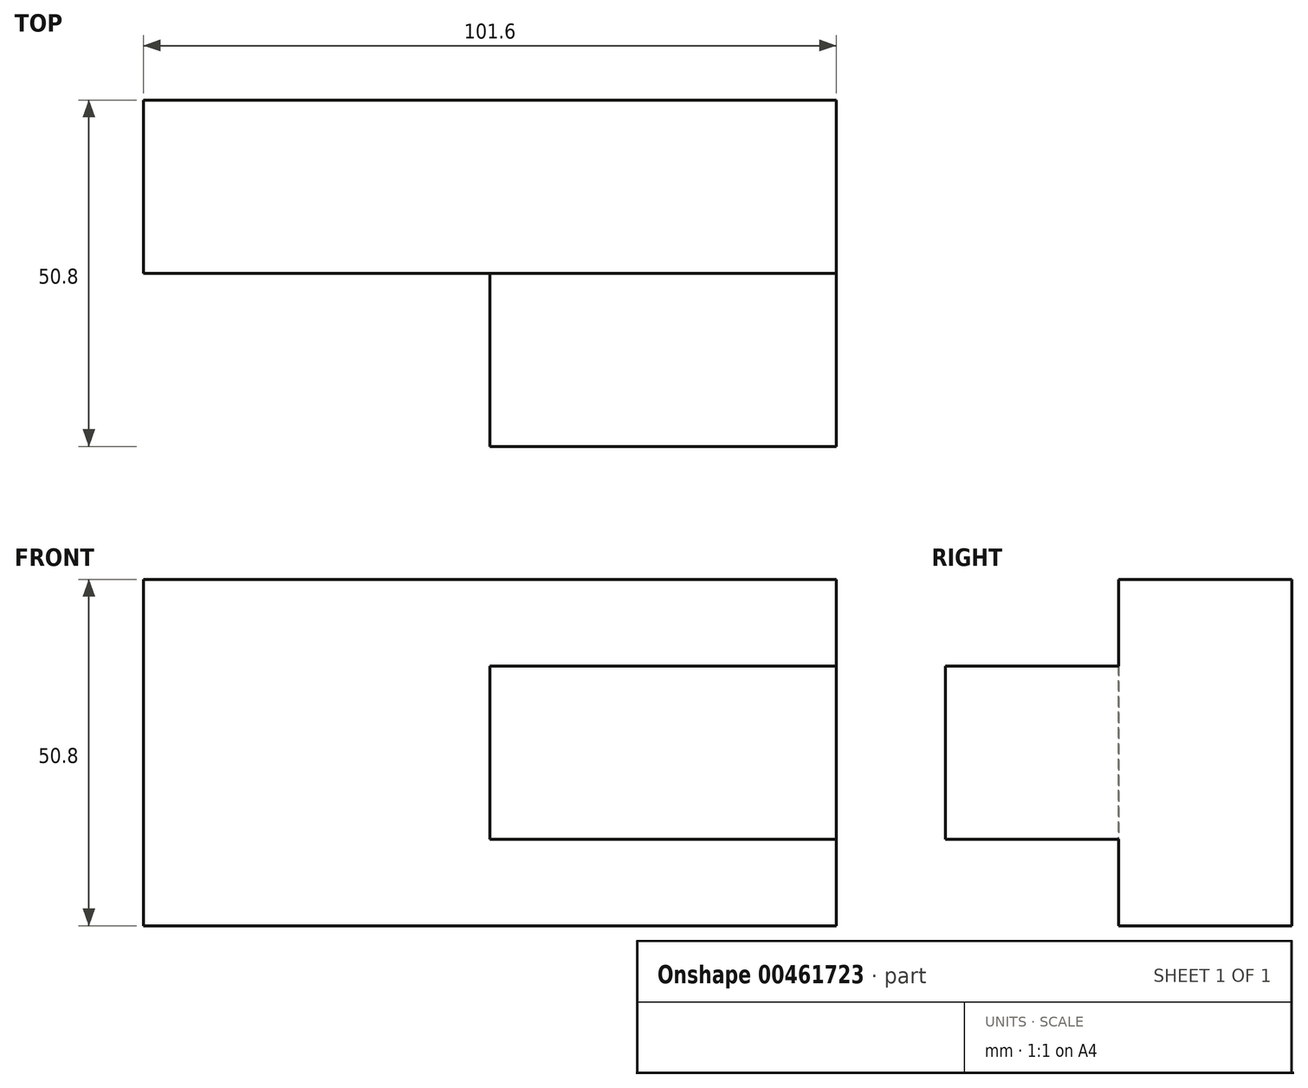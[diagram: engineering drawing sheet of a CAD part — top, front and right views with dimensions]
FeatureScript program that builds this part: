
annotation { "Feature Type Name" : "Feature", "Feature Type Description" : "" }
export const myFeature = defineFeature(function(context is Context, id is Id, definition is map)
    precondition{}
    {
        {
            var Q0;
            Q0=qCreatedBy(makeId("Front.planeOp"),FACE);
            var sketch = newSketch(context, id + "F0", { "sketchPlane" : qUnion([Q0])});
            skLineSegment(sketch, "E0.bottom", {"start": v(50.8, -25.4) * mm, "end": v(-50.8, -25.4) * mm});
            skLineSegment(sketch, "E0.top", {"start": v(50.8, 25.4) * mm, "end": v(-50.8, 25.4) * mm});
            skLineSegment(sketch, "E0.left", {"start": v(50.8, -25.4) * mm, "end": v(50.8, 25.4) * mm});
            skLineSegment(sketch, "E0.right", {"start": v(-50.8, -25.4) * mm, "end": v(-50.8, 25.4) * mm});
            skPoint(sketch, "E0.middle", {"position": v(0, 0) * mm});
            skSolve(sketch);
        }
        {
            var Q0;
            Q0 = qSketchRegion(id + "F0", true);
            extrude(context, id + "F1", {"entities" : qUnion([Q0]), "depth" : 25.4 * mm});
        }
        {
            var Q0;
            Q0=makeQuery(id+"F1.opExtrude","CAP_FACE",FACE,{"disambiguationData":[OSD([sQuery(id+"F0.wireOp",EDGE,"E0.bottom"),sQuery(id+"F0.wireOp",EDGE,"E0.top"),sQuery(id+"F0.wireOp",EDGE,"E0.left"),sQuery(id+"F0.wireOp",EDGE,"E0.right")])],"isStart":false});
            var sketch = newSketch(context, id + "F2", { "sketchPlane" : qUnion([Q0])});
            skLineSegment(sketch, "E1.bottom", {"start": v(50.8, 12.7) * mm, "end": v(0, 12.7) * mm});
            skLineSegment(sketch, "E1.top", {"start": v(50.8, -12.7) * mm, "end": v(0, -12.7) * mm});
            skLineSegment(sketch, "E1.left", {"start": v(50.8, 12.7) * mm, "end": v(50.8, -12.7) * mm});
            skLineSegment(sketch, "E1.right", {"start": v(0, 12.7) * mm, "end": v(0, -12.7) * mm});
            skSolve(sketch);
        }
        {
            var Q0;
            Q0=makeQuery(id+"F2.imprint","IMPRINT",FACE,{"disambiguationData":[TD([[makeQuery(id+"F2.imprint","IMPRINT",EDGE,{"derivedFrom":sQuery(id+"F2.wireOp",EDGE,"E1.bottom")}),1.0]])]});
            extrude(context, id + "F3", {"entities" : qUnion([Q0]), "operationType" : NewBodyOperationType.ADD, "depth" : 25.4 * mm});
        }
    });
